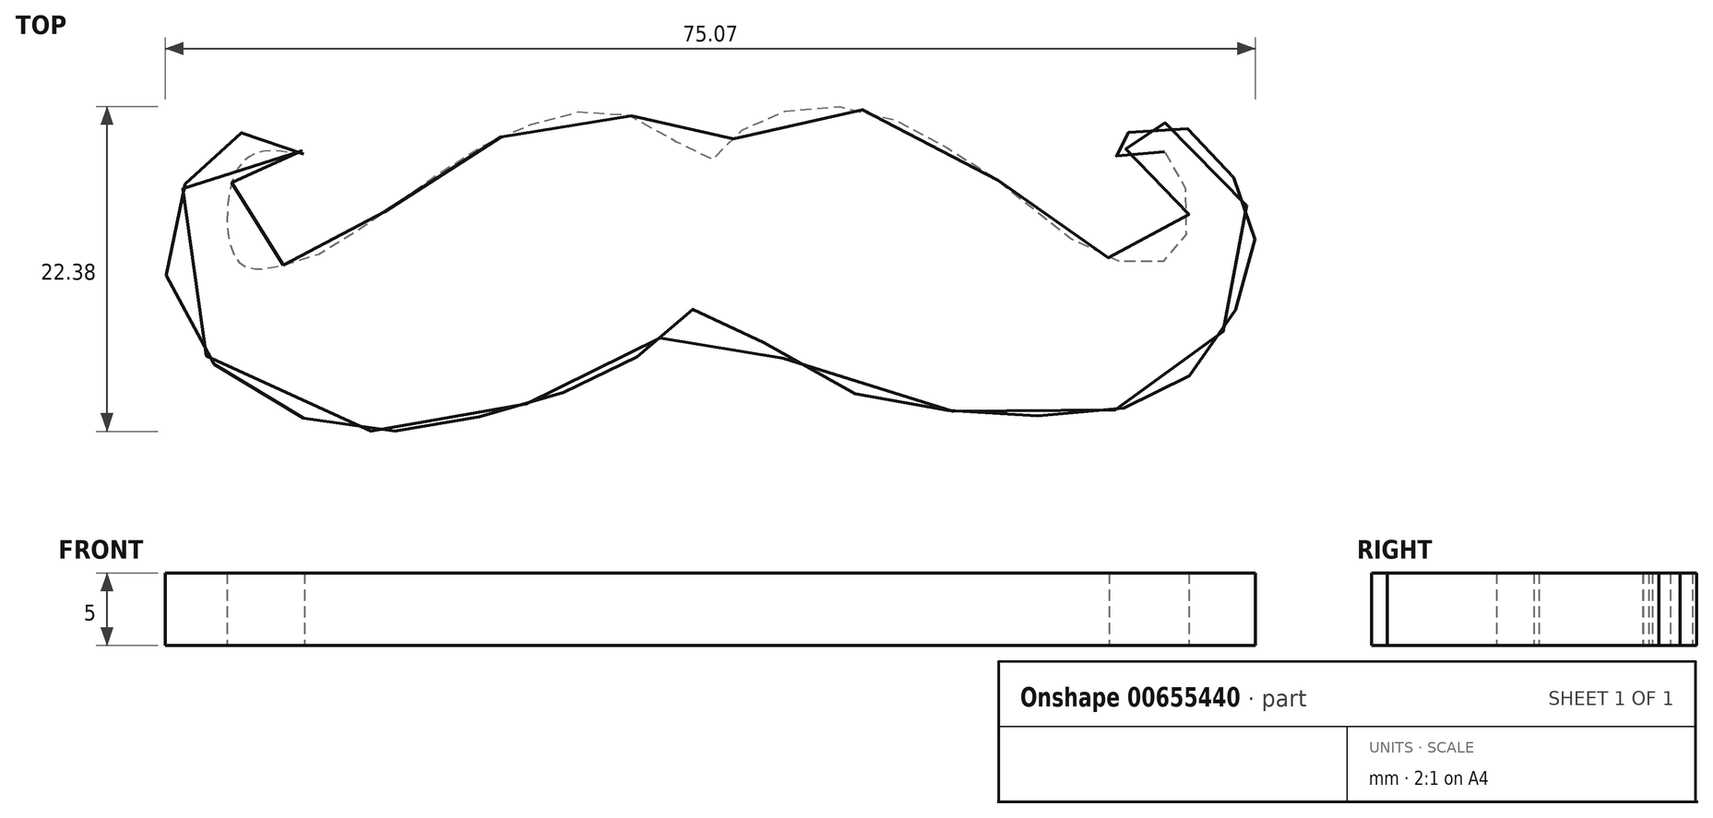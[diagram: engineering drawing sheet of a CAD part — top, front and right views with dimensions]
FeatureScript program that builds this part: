
annotation { "Feature Type Name" : "Feature", "Feature Type Description" : "" }
export const myFeature = defineFeature(function(context is Context, id is Id, definition is map)
    precondition{}
    {
        {
            var Q0;
            Q0=qCreatedBy(makeId("Top.planeOp"),FACE);
            var sketch = newSketch(context, id + "F0", { "sketchPlane" : qUnion([Q0])});
            skFitSpline(sketch, "E0", {"points": [v(-66.7, 11.17) * mm, v(-64.4, 11.87) * mm, v(-61.3, 13.78) * mm, v(-57.68, 16.29) * mm, v(-53.67, 19) * mm, v(-49.56, 20.9) * mm, v(-45.25, 21.81) * mm, v(-40.73, 20.5) * mm, v(-37.42, 18.4) * mm, v(-35.42, 20.2) * mm, v(-31.95, 21.81) * mm, v(-26.55, 21.81) * mm, v(-21.08, 19.3) * mm, v(-16.66, 16.39) * mm, v(-13.56, 13.78) * mm, v(-9.24, 11.47) * mm, v(-5.83, 11.57) * mm, v(-4.53, 13.28) * mm, v(-4.73, 16.99) * mm, v(-6.48, 19.28) * mm, v(-8.64, 19.2) * mm, v(-9.77, 18.44) * mm, v(-9.54, 19.4) * mm, v(-6.94, 20.9) * mm, v(-4.13, 20.4) * mm, v(-1.52, 17.6) * mm, v(0, 14.08) * mm, v(0, 10.9) * mm, v(-2.69, 5.54) * mm, v(-5.63, 2.55) * mm, v(-10.45, 1.04) * mm, v(-16.97, 0.84) * mm, v(-23.79, 1.54) * mm, v(-31.4, 4.15) * mm, v(-37.6, 8.32) * mm, v(-40.64, 6.3) * mm, v(-44.75, 3.45) * mm, v(-50.56, 1.44) * mm, v(-56.58, 0) * mm, v(-62.9, 0) * mm, v(-70.72, 3.65) * mm, v(-74.82, 10.9) * mm, v(-72.93, 17.7) * mm, v(-69.22, 20.3) * mm, v(-65.26, 18.86) * mm, v(-66.95, 19.03) * mm, v(-69.23, 18.53) * mm, v(-70.5, 15.74) * mm, v(-69.65, 11.27) * mm, v(-66.7, 11.17) * mm]});
            skSolve(sketch);
        }
        {
            var Q0;
            Q0 = qSketchRegion(id + "F0", true);
            extrude(context, id + "F1", {"entities" : qUnion([Q0]), "depth" : 5 * mm, "offsetDistance" : 25 * mm});
        }
    });
